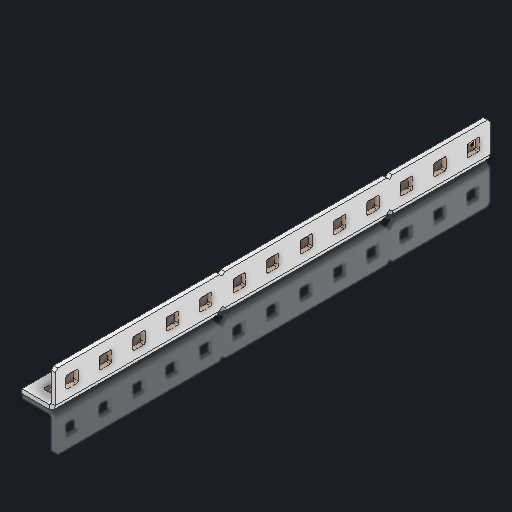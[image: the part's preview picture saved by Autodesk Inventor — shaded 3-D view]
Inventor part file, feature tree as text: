
AUTODESK INVENTOR PART (.ipt)
format: ipt  version: 2023.2 (Build 272271030, 271C)  size: 562,688 bytes
history: native  units: in
note: dims shown in document units (in); Inventor stores cm internally (conversion verified against a paired STEP export)
features: other x31, extrude x25, sheet_metal_op x10, sketch x8, mirror x1, pattern_linear x1, chamfer x1
ambient origin geometry x8: Origin, YZ Plane, XZ Plane, XY Plane, X Axis, Y Axis, Z Axis, Center Point
bodies: Solid1 (feature_tree), Body (feature_tree)
feature tree (77):
  other  "Flange Pattern Plane"
  sheet_metal_op  "Flange Pattern"
  sheet_metal_op  "Body Pattern"
  other  "Arc Length"
  mirror  "Notch Mirror"
  pattern_linear  "Notch Pattern"  Spacing1=0.25in  [1 undecoded]
  chamfer  "End Chamfer"
  extrude  "Half Cut"  Depth=0.0625in
  sketch  "Sketch1"  dims[d0=1.5in]
  other  "Plate1"
  sketch  "Sketch2"  dims[d1=6.5in]
  other  "Plate2"
  sheet_metal_op  "Bend1"
  sheet_metal_op  "Corner1"
  sketch  "Sketch3"  dims[d2=0.0625in]
  other  "Flange Pattern Sketch"
  sketch  "Sketch7"  dims[d3=0.0625in]
  other  "Srf1"
  other  "Srf2"
  sketch  "Sketch8"  dims[d4=0.0312in]
  sketch  "Sketch9"  dims[d5=0.125in]
  other  "Srf91"
  sheet_metal_op  "Body Pattern Sketch"
  other  "Srf92"
  sketch  "Sketch13"  dims[d6=0.0625in]
  sketch  "Sketch14"  dims[d7=0.5in d8=90.0deg d9=0.0312in d10=0.25in d11=0.0625in d12=0.0625in d16=0.182in d17=0.02in d18=0.0625in d19=0.0in d20=0.25in d21=0.25in d46=0.172in d47=1.0in d48=0.0in d49=0.182in d50=0.02in d51=0.25in d52=0.25in d53=0.0625in d54=0.0in d55=0.172in d56=1.0in d57=0.0in d60=5.1181in d62=0.5in d63=0.3937in d65=0.5in d85=0.1473in d86=0.1782in d88=0.04in d89=0.0625in d90=0.0in d91=0.04in d92=0.0491in d95=2.5in d96=0.04in d97=0.25in d98=45.0deg d101=0.0in d102=2.497in d131=0.5in d132=5.1181in d134=0.5in d139=0.5in]
  other  "Srf856"
  other  "Srf1310"
  other  "Srf1311"
  other  "Srf1312"
  other  "Srf1376"
  other  "Srf1377"
  other  "Srf1728"
  other  "Srf1755"
  other  "Srf1878"
  other  "Srf1879"
  other  "Srf1880"
  other  "Srf1881"
  other  "Srf1882"
  other  "Srf1883"
  other  "Srf1884"
  other  "Srf1942"
  other  "Srf1943"
  other  "Srf1944"
  other  "Srf1945"
  other  "Srf1946"
  other  "Srf1947"
  other  "Srf1948"
  sheet_metal_op  "Flange Stamp"
  sheet_metal_op  "Flange Circle"
  sheet_metal_op  "Body Stamp"
  sheet_metal_op  "Body Circle"
  sheet_metal_op  "Notch"
  extrude  "ExtrusionSrf2"  Depth=0.0625in
  extrude  "ExtrusionSrf92"  Depth=0.5in
  extrude  "ExtrusionSrf856"  Depth=0.02in
  extrude  "ExtrusionSrf1310"  Depth=0.0625in
  extrude  "ExtrusionSrf1311"  TaperAngle=0.0deg  [1 undecoded]
  extrude  "ExtrusionSrf1312"  Depth=0.5in
  extrude  "ExtrusionSrf1376"  Depth=0.5in
  extrude  "ExtrusionSrf1377"  Depth=0.5in
  extrude  "ExtrusionSrf1728"  Depth=0.5in TaperAngle=0.0deg
  extrude  "ExtrusionSrf1755"  Depth=0.5in
  extrude  "ExtrusionSrf1878"  Depth=0.02in
  extrude  "ExtrusionSrf1879"  Depth=0.5in
  extrude  "ExtrusionSrf1880"  Depth=0.5in
  extrude  "ExtrusionSrf1881"  Depth=0.0625in
  extrude  "ExtrusionSrf1882"  TaperAngle=0.0deg  [1 undecoded]
  extrude  "ExtrusionSrf1883"  Depth=0.5in
  extrude  "ExtrusionSrf1884"  Depth=0.5in TaperAngle=0.0deg
  extrude  "ExtrusionSrf1942"  Depth=0.5in
  extrude  "ExtrusionSrf1943"  Depth=0.5in
  extrude  "ExtrusionSrf1944"  Depth=0.5in
  extrude  "ExtrusionSrf1945"  Depth=0.5in
  extrude  "ExtrusionSrf1946"  Depth=0.5in
  extrude  "ExtrusionSrf1947"  Depth=0.0625in
  extrude  "ExtrusionSrf1948"  TaperAngle=0.0deg  [1 undecoded]
note: 4 required parameter values undecoded (feature->parameter linkage not recoverable at this tier; creation-order binding heuristic only, values carry confidence <= 0.55)
